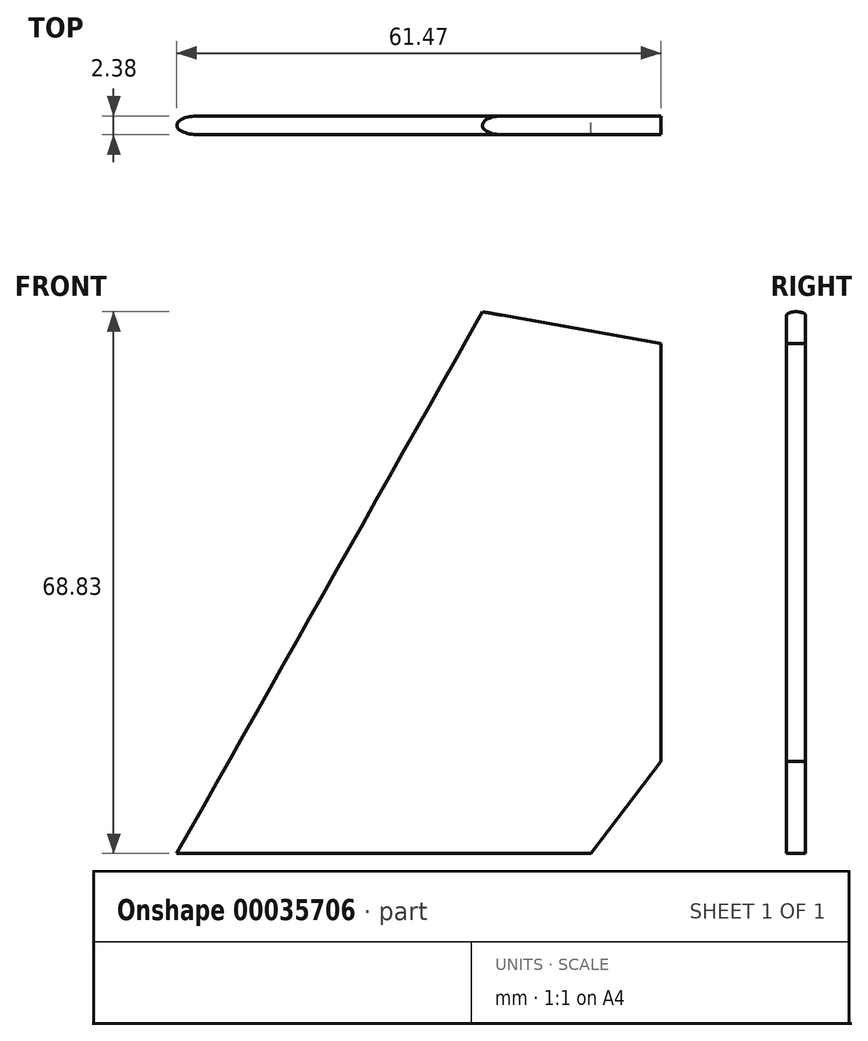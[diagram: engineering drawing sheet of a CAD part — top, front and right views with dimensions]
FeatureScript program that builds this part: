
annotation { "Feature Type Name" : "Feature", "Feature Type Description" : "" }
export const myFeature = defineFeature(function(context is Context, id is Id, definition is map)
    precondition{}
    {
        {
            var Q0;
            Q0=qCreatedBy(makeId("Front.planeOp"),FACE);
            var sketch = newSketch(context, id + "F0", { "sketchPlane" : qUnion([Q0])});
            skLineSegment(sketch, "E0", {"start": v(59.18, 0) * mm, "end": v(0, 0) * mm});
            skLineSegment(sketch, "E1", {"start": v(61.47, 64.82) * mm, "end": v(61.47, 11.68) * mm});
            skLineSegment(sketch, "E2", {"start": v(56.13, 57.67) * mm, "end": v(56.13, 11.68) * mm});
            skLineSegment(sketch, "E3", {"start": v(68.07, 73.15) * mm, "end": v(68.07, 11.68) * mm});
            skLineSegment(sketch, "E4", {"start": v(68.07, 11.68) * mm, "end": v(6.59, 11.68) * mm, "construction": true});
            skLineSegment(sketch, "E5", {"start": v(43.69, 77.47) * mm, "end": v(68.07, 73.15) * mm});
            skLineSegment(sketch, "E6", {"start": v(0, 0) * mm, "end": v(43.69, 77.47) * mm});
            skLineSegment(sketch, "E7", {"start": v(34.66, 61.47) * mm, "end": v(56.13, 57.67) * mm});
            skLineSegment(sketch, "E8", {"start": v(56.13, 11.68) * mm, "end": v(47.24, 0) * mm});
            skLineSegment(sketch, "E9", {"start": v(61.47, 11.68) * mm, "end": v(52.58, 0) * mm});
            skLineSegment(sketch, "E10", {"start": v(38.82, 68.83) * mm, "end": v(61.47, 64.82) * mm});
            skLineSegment(sketch, "E11", {"start": v(68.07, 11.68) * mm, "end": v(59.18, 0) * mm});
            skSolve(sketch);
        }
        {
            var Q0;
            Q0=makeQuery(id+"F0.imprint","IMPRINT",FACE,{"disambiguationData":[TD([[makeQuery(id+"F0.imprint","IMPRINT",EDGE,{"derivedFrom":sQuery(id+"F0.wireOp",EDGE,"E2")}),-1.0]])]});
            var Q1;
            Q1=makeQuery(id+"F0.imprint","IMPRINT",FACE,{"disambiguationData":[TD([[makeQuery(id+"F0.imprint","IMPRINT",EDGE,{"derivedFrom":sQuery(id+"F0.wireOp",EDGE,"E1")}),-1.0]])]});
            extrude(context, id + "F1", {"entities" : qUnion([Q0, Q1]), "depth" : 2.38 * mm, "symmetric" : true});
        }
        {
            var Q0;
            Q0=sQuery(id+"F0.wireOp",EDGE,"E6");
            var Q1;
            Q1=sQuery(id+"F0.wireOp",VERTEX,"E6.start");
            cPlane(context, id + "F2", {"entities" : qUnion([Q0, Q1]), "cplaneType" : CPlaneType.LINE_POINT, "offset" : 152.4 * mm, "width" : 152.4 * mm, "height" : 152.4 * mm});
        }
        {
            var Q0;
            Q0=qCreatedBy(id+"F2.planeOp",FACE);
            var sketch = newSketch(context, id + "F3", { "sketchPlane" : qUnion([Q0])});
            skLineSegment(sketch, "E12.2", {"start": v(2.38, -1.2) * mm, "end": v(21.7, -1.2) * mm});
            skLineSegment(sketch, "E13", {"start": v(21.7, 1.2) * mm, "end": v(21.7, 12.7) * mm});
            skLineSegment(sketch, "E14", {"start": v(21.7, 12.7) * mm, "end": v(-12.7, 12.7) * mm});
            skLineSegment(sketch, "E15", {"start": v(-12.7, 12.7) * mm, "end": v(-12.7, -12.7) * mm});
            skLineSegment(sketch, "E16", {"start": v(-12.7, -12.7) * mm, "end": v(21.7, -12.7) * mm});
            skLineSegment(sketch, "E12.1", {"start": v(2.38, 1.2) * mm, "end": v(21.7, 1.2) * mm});
            skPoint(sketch, "E17.orphan", {"position": v(0, 1.2) * mm});
            skLineSegment(sketch, "E18", {"start": v(21.7, -12.7) * mm, "end": v(21.7, -1.2) * mm});
            skLineSegment(sketch, "E19", {"start": v(0, 0) * mm, "end": v(2.38, 0) * mm});
            skEllipticalArc(sketch, "E20", {});
            skLineSegment(sketch, "E21", {"start": v(2.38, 0) * mm, "end": v(0, 0) * mm, "construction": true});
            skLineSegment(sketch, "E22", {"start": v(2.38, 1.2) * mm, "end": v(2.38, -1.2) * mm, "construction": true});
            const initialGuessF3  = {"E20": [0.00238125, 0, -1, 0, 0.0023812499999999875, 0.001190625, 4.71238898038469, 1.5707963267948966]};
            skSetInitialGuess(sketch, initialGuessF3);
            skSolve(sketch);
        }
        {
            var Q0;
            Q0 = qSketchRegion(id + "F3", true);
            extrude(context, id + "F4", {"entities" : qUnion([Q0]), "operationType" : NewBodyOperationType.REMOVE, "endBound" : BoundingType.THROUGH_ALL, "depth" : 25.4 * mm});
        }
    });
